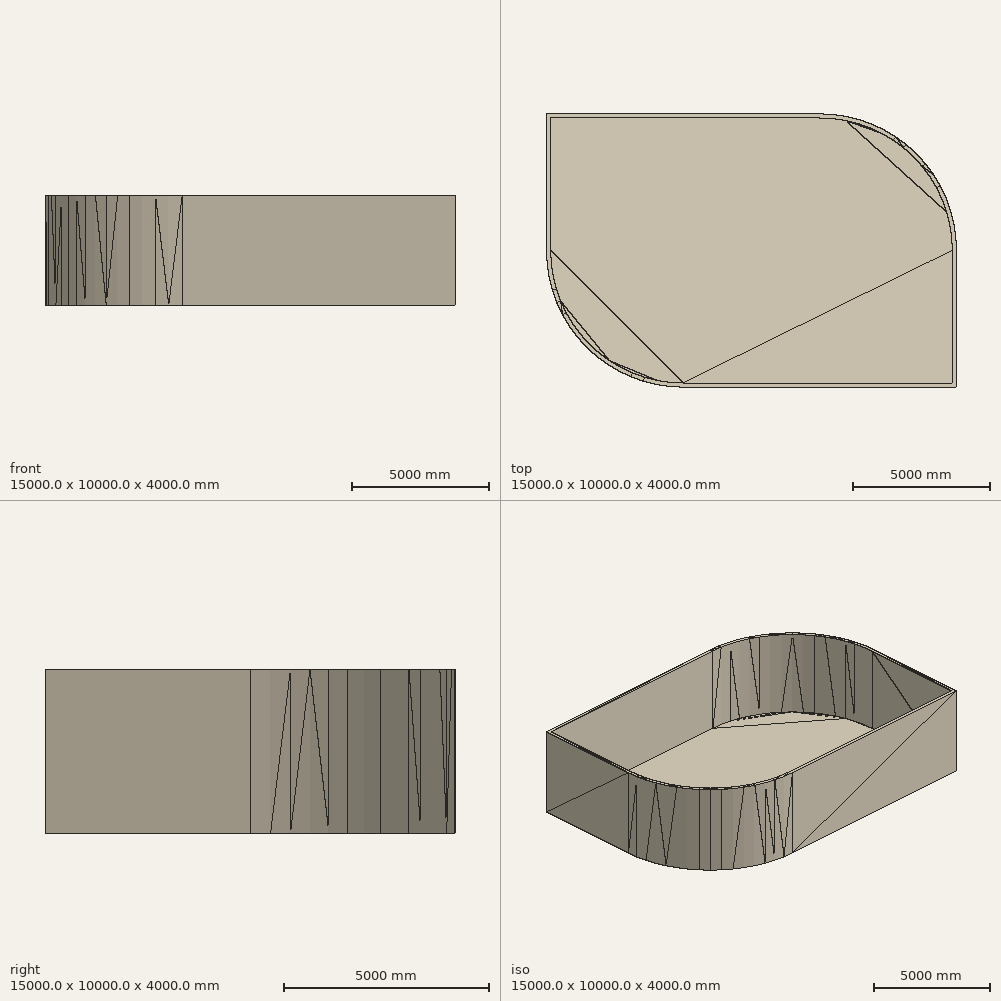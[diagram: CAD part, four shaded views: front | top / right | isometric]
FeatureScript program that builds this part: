
annotation { "Feature Type Name" : "Feature", "Feature Type Description" : "" }
export const myFeature = defineFeature(function(context is Context, id is Id, definition is map)
    precondition{}
    {
        {
            var Q0;
            Q0=qCreatedBy(makeId("Top.planeOp"),FACE);
            var sketch = newSketch(context, id + "F0", { "sketchPlane" : qUnion([Q0])});
            skLineSegment(sketch, "E0.bottom", {"start": v(-11945.68, 4850.04) * mm, "end": v(-1945.68, 4850.04) * mm});
            skLineSegment(sketch, "E0.top", {"start": v(-6945.68, -5149.96) * mm, "end": v(3054.32, -5149.96) * mm});
            skLineSegment(sketch, "E0.left", {"start": v(-11945.68, 4850.04) * mm, "end": v(-11945.68, -149.96) * mm});
            skLineSegment(sketch, "E0.right", {"start": v(3054.32, -149.96) * mm, "end": v(3054.32, -5149.96) * mm});
            skPoint(sketch, "E1.visualSharp", {"position": v(-11945.68, 4850.04) * mm});
            skLineSegment(sketch, "E1.filletArc", {"start": v(-11945.68, 4850.04) * mm, "end": v(-11945.68, 4850.04) * mm});
            skPoint(sketch, "E2.visualSharp", {"position": v(3054.32, -5149.96) * mm});
            skLineSegment(sketch, "E2.filletArc", {"start": v(3054.32, -5149.96) * mm, "end": v(3054.32, -5149.96) * mm});
            skPoint(sketch, "E3.visualSharp", {"position": v(-11945.68, -5149.96) * mm});
            skArc(sketch, "E3.filletArc", {"start": v(-11945.68, -149.96) * mm, "mid": v(-10481.21, -3685.5) * mm, "end": v(-6945.68, -5149.96) * mm});
            skPoint(sketch, "E4.visualSharp", {"position": v(3054.32, 4850.04) * mm});
            skArc(sketch, "E4.filletArc", {"start": v(3054.32, -149.96) * mm, "mid": v(1589.86, 3385.58) * mm, "end": v(-1945.68, 4850.04) * mm});
            skPoint(sketch, "E5.firstSnap0", {"position": v(-11945.68, 2350.04) * mm});
            skLineSegment(sketch, "E6", {"start": v(-6945.68, -149.96) * mm, "end": v(-6945.68, -2149.96) * mm});
            skLineSegment(sketch, "E7", {"start": v(-6945.68, -5149.96) * mm, "end": v(-6945.68, -3149.96) * mm});
            skLineSegment(sketch, "E8", {"start": v(-11945.68, -149.96) * mm, "end": v(-6945.68, -149.96) * mm});
            skSolve(sketch);
        }
        {
            var Q0;
            Q0=makeQuery(id+"F0.imprint","IMPRINT",FACE,{"disambiguationData":[TD([[makeQuery(id+"F0.imprint","IMPRINT",EDGE,{"derivedFrom":sQuery(id+"F0.wireOp",EDGE,"E0.bottom")}),-1.0]])]});
            extrude(context, id + "F1", {"entities" : qUnion([Q0]), "depth" : 4000 * mm, "offsetDistance" : 25.4 * mm});
        }
        {
            var Q0;
            Q0=makeQuery(id+"F1.opExtrude","CAP_FACE",FACE,{"disambiguationData":[OSD([sQuery(id+"F0.wireOp",EDGE,"E0.bottom"),sQuery(id+"F0.wireOp",EDGE,"E0.top"),sQuery(id+"F0.wireOp",EDGE,"E0.left"),sQuery(id+"F0.wireOp",EDGE,"E0.right"),sQuery(id+"F0.wireOp",EDGE,"E1.filletArc"),sQuery(id+"F0.wireOp",EDGE,"E2.filletArc")])],"isStart":false});
            shell(context, id + "F2", {"entities" : qUnion([Q0]), "thickness" : 152.4 * mm});
        }
        {
            var Q0;
            Q0=sQuery(id+"F0.wireOp",EDGE,"E6");
            extrude(context, id + "F3", {"bodyType" : ToolBodyType.SURFACE, "surfaceEntities" : qUnion([Q0]), "depth" : 4000 * mm, "offsetDistance" : 25.4 * mm});
        }
        {
            var Q0;
            Q0=sQuery(id+"F0.wireOp",EDGE,"E7");
            extrude(context, id + "F4", {"bodyType" : ToolBodyType.SURFACE, "surfaceEntities" : qUnion([Q0]), "depth" : 4000 * mm, "offsetDistance" : 25.4 * mm});
        }
    });
